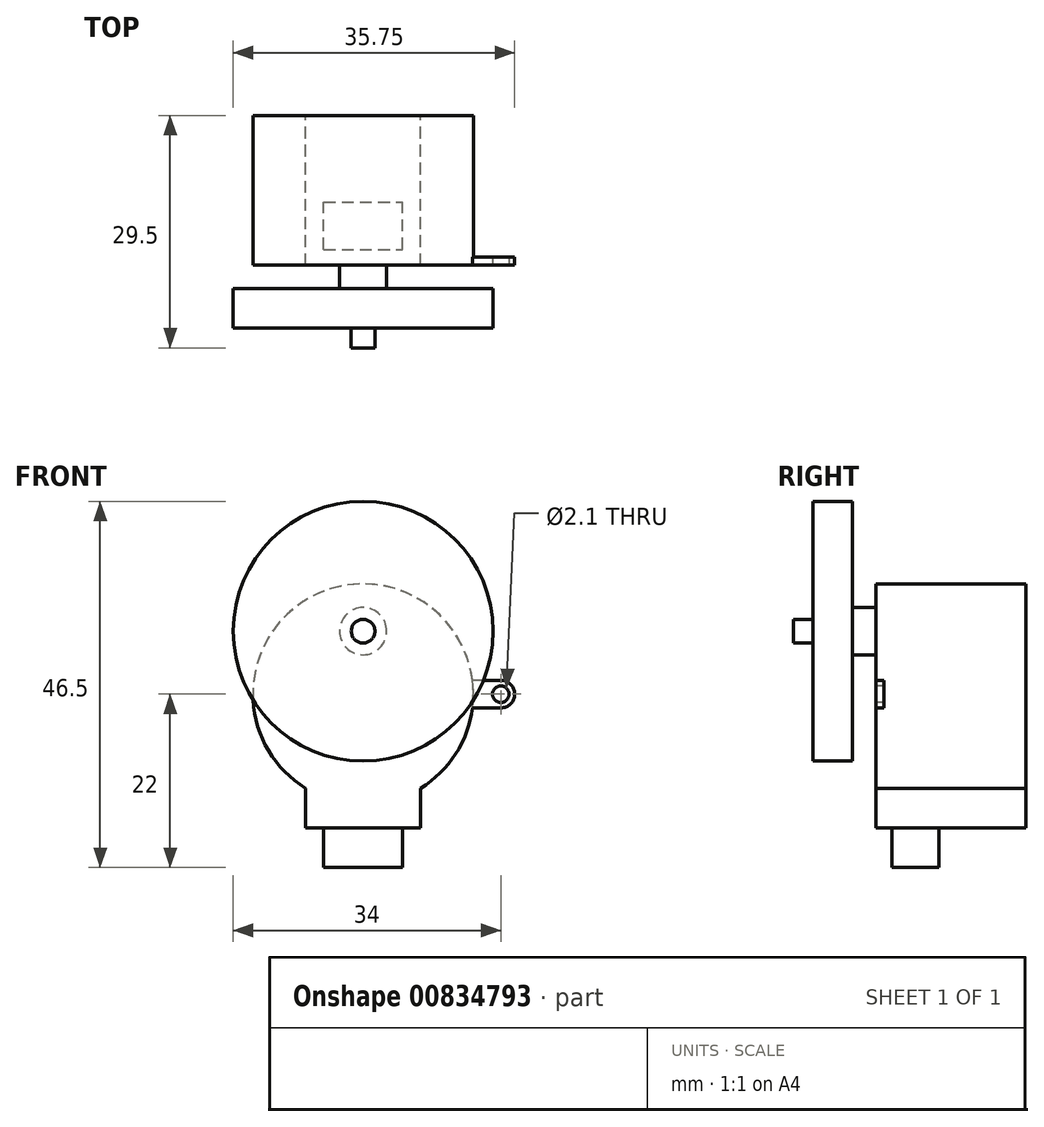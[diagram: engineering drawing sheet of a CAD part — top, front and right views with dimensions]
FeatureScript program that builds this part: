
annotation { "Feature Type Name" : "Feature", "Feature Type Description" : "" }
export const myFeature = defineFeature(function(context is Context, id is Id, definition is map)
    precondition{}
    {
        {
            var Q0;
            Q0=qCreatedBy(makeId("Front.planeOp"),FACE);
            var sketch = newSketch(context, id + "F0", { "sketchPlane" : qUnion([Q0])});
            skArc(sketch, "E0", {"start": v(7.3, -11.95) * mm, "mid": v(0, 14) * mm, "end": v(-7.3, -11.95) * mm});
            skLineSegment(sketch, "E1.top", {"start": v(-7.3, -17) * mm, "end": v(7.3, -17) * mm});
            skLineSegment(sketch, "E1.left", {"start": v(-7.3, -11.95) * mm, "end": v(-7.3, -17) * mm});
            skLineSegment(sketch, "E1.right", {"start": v(7.3, -11.95) * mm, "end": v(7.3, -17) * mm});
            skLineSegment(sketch, "E2", {"start": v(0, 0) * mm, "end": v(0, -8.8) * mm, "construction": true});
            skSolve(sketch);
        }
        {
            var Q0;
            Q0 = qSketchRegion(id + "F0", true);
            extrude(context, id + "F1", {"entities" : qUnion([Q0]), "depth" : 19 * mm, "offsetDistance" : 25 * mm});
        }
        {
            var Q0;
            Q0=makeQuery(id+"F1.opExtrude","CAP_FACE",FACE,{"disambiguationData":[OSD([sQuery(id+"F0.wireOp",EDGE,"E0"),sQuery(id+"F0.wireOp",EDGE,"E1.top"),sQuery(id+"F0.wireOp",EDGE,"E1.left"),sQuery(id+"F0.wireOp",EDGE,"E1.right")])],"isStart":false});
            var sketch = newSketch(context, id + "F2", { "sketchPlane" : qUnion([Q0])});
            skCircle(sketch, "E3", {"center": v(0, 8) * mm, "radius": 3 * mm});
            skSolve(sketch);
        }
        {
            var Q0;
            Q0 = qSketchRegion(id + "F2", true);
            extrude(context, id + "F3", {"entities" : qUnion([Q0]), "operationType" : NewBodyOperationType.ADD, "depth" : 3 * mm, "offsetDistance" : 25 * mm});
        }
        {
            var Q0;
            Q0=makeQuery(id+"F3.opExtrude","CAP_FACE",FACE,{"disambiguationData":[OSD([sQuery(id+"F2.wireOp",EDGE,"E3")])],"isStart":false});
            var sketch = newSketch(context, id + "F4", { "sketchPlane" : qUnion([Q0])});
            skCircle(sketch, "E4", {"center": v(0, 8) * mm, "radius": 1.5 * mm});
            skSolve(sketch);
        }
        {
            var Q0;
            Q0 = qSketchRegion(id + "F4", true);
            extrude(context, id + "F5", {"entities" : qUnion([Q0]), "operationType" : NewBodyOperationType.ADD, "depth" : 7.5 * mm, "offsetDistance" : 25 * mm});
        }
        {
            var Q0;
            Q0=makeQuery(id+"F1.opExtrude","CAP_FACE",FACE,{"disambiguationData":[OSD([sQuery(id+"F0.wireOp",EDGE,"E0"),sQuery(id+"F0.wireOp",EDGE,"E1.top"),sQuery(id+"F0.wireOp",EDGE,"E1.left"),sQuery(id+"F0.wireOp",EDGE,"E1.right")])],"isStart":false});
            var sketch = newSketch(context, id + "F6", { "sketchPlane" : qUnion([Q0])});
            skCircle(sketch, "E5", {"center": v(17.5, 0) * mm, "radius": 1.05 * mm});
            skArc(sketch, "E6", {"start": v(17.5, -1.75) * mm, "mid": v(19.25, 0) * mm, "end": v(17.5, 1.75) * mm});
            skLineSegment(sketch, "E7", {"start": v(17.5, 1.75) * mm, "end": v(13.9, 1.75) * mm});
            skLineSegment(sketch, "E8", {"start": v(17.5, -1.75) * mm, "end": v(13.9, -1.75) * mm});
            skLineSegment(sketch, "E9", {"start": v(13.9, 1.75) * mm, "end": v(13.9, -1.75) * mm});
            skSolve(sketch);
        }
        {
            var Q0;
            Q0 = qSketchRegion(id + "F6", true);
            extrude(context, id + "F7", {"entities" : qUnion([Q0]), "operationType" : NewBodyOperationType.ADD, "oppositeDirection" : true, "depth" : 1 * mm, "offsetDistance" : 25 * mm});
        }
        {
            var Q0;
            Q0=makeQuery(id+"F3.opExtrude","CAP_FACE",FACE,{"disambiguationData":[OSD([sQuery(id+"F2.wireOp",EDGE,"E3")])],"isStart":false});
            var sketch = newSketch(context, id + "F8", { "sketchPlane" : qUnion([Q0])});
            skCircle(sketch, "E10", {"center": v(0, 8) * mm, "radius": 16.5 * mm});
            skSolve(sketch);
        }
        {
            var Q0;
            Q0 = qSketchRegion(id + "F8", true);
            extrude(context, id + "F9", {"entities" : qUnion([Q0]), "operationType" : NewBodyOperationType.ADD, "depth" : 5 * mm, "offsetDistance" : 25 * mm});
        }
        {
            var Q0;
            Q0=makeQuery(id+"F1.opExtrude","SWEPT_FACE",FACE,{"disambiguationData":[OSD([sQuery(id+"F0.wireOp",EDGE,"E1.top")])]});
            var sketch = newSketch(context, id + "F10", { "sketchPlane" : qUnion([Q0])});
            skLineSegment(sketch, "E11.bottom", {"start": v(-5, 17) * mm, "end": v(5, 17) * mm});
            skLineSegment(sketch, "E11.top", {"start": v(-5, 11) * mm, "end": v(5, 11) * mm});
            skLineSegment(sketch, "E11.left", {"start": v(-5, 17) * mm, "end": v(-5, 11) * mm});
            skLineSegment(sketch, "E11.right", {"start": v(5, 17) * mm, "end": v(5, 11) * mm});
            skPoint(sketch, "E12", {"position": v(0, 19) * mm});
            skPoint(sketch, "E13", {"position": v(0, 17) * mm});
            skSolve(sketch);
        }
        {
            var Q0;
            Q0 = qSketchRegion(id + "F10", true);
            extrude(context, id + "F11", {"entities" : qUnion([Q0]), "operationType" : NewBodyOperationType.ADD, "depth" : 5 * mm, "offsetDistance" : 25 * mm});
        }
    });
